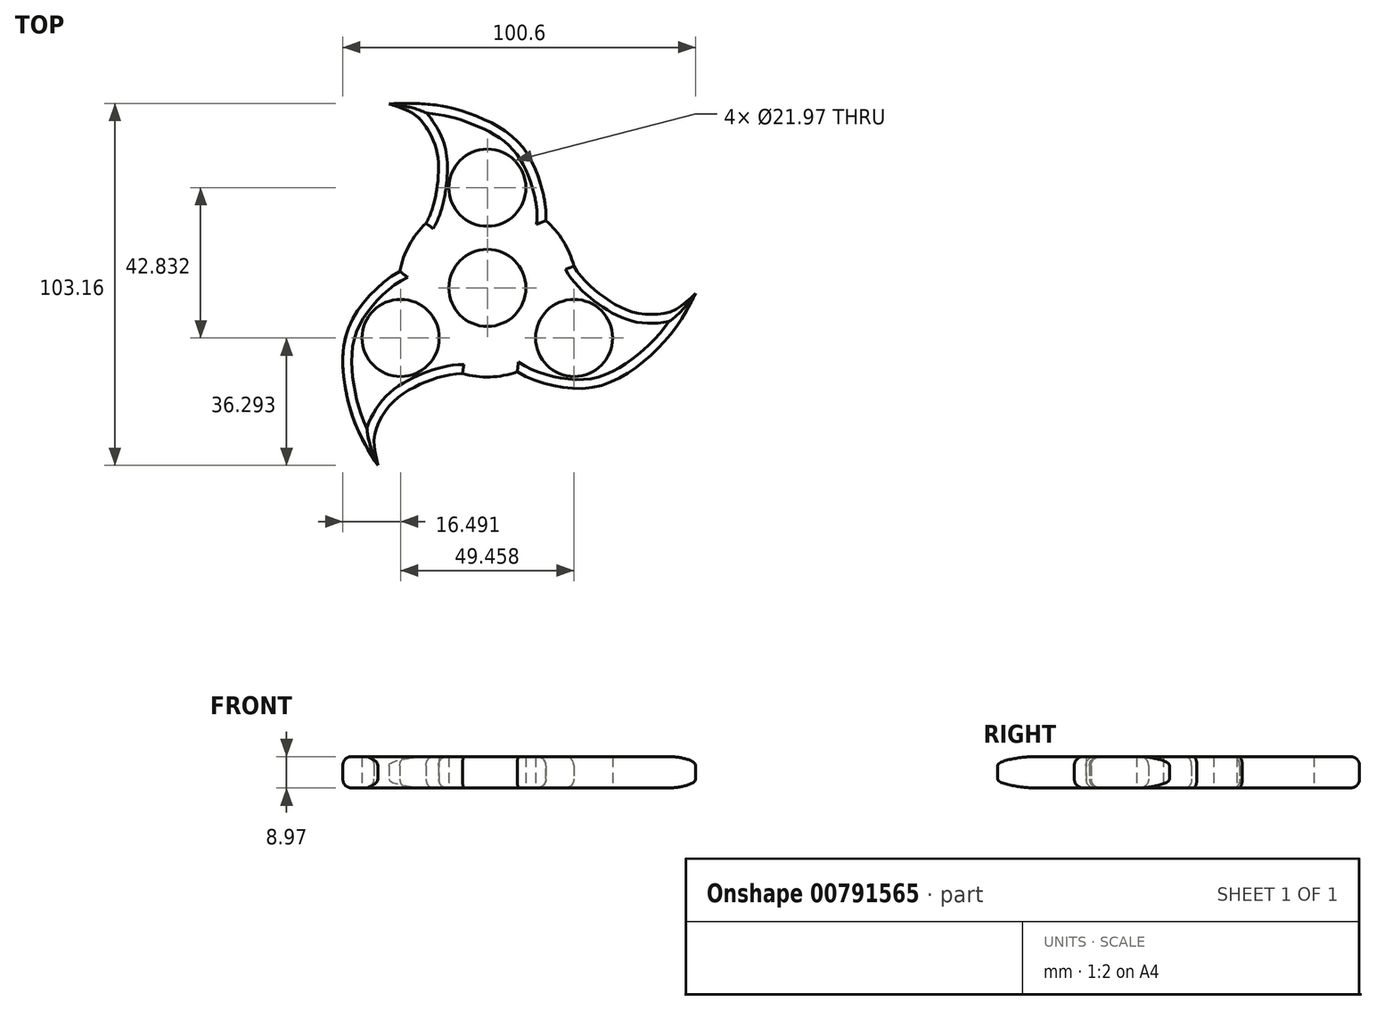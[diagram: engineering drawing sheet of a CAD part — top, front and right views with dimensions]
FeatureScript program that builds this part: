
annotation { "Feature Type Name" : "Feature", "Feature Type Description" : "" }
export const myFeature = defineFeature(function(context is Context, id is Id, definition is map)
    precondition{}
    {
        {
            var Q0;
            Q0=qCreatedBy(makeId("Top.planeOp"),FACE);
            var sketch = newSketch(context, id + "F0", { "sketchPlane" : qUnion([Q0])});
            skCircle(sketch, "E0", {"center": v(0, 0) * mm, "radius": 10.99 * mm});
            skCircle(sketch, "E1", {"center": v(0, 0) * mm, "radius": 25.4 * mm});
            skLineSegment(sketch, "E2", {"start": v(-2.48, 0) * mm, "end": v(2.46, 0) * mm, "construction": true});
            skLineSegment(sketch, "E3", {"start": v(0, 2.4) * mm, "end": v(0, -2.3) * mm});
            skFitSpline(sketch, "E4", {"points": [v(-28.09, 52.42) * mm, v(-3.88, 49.24) * mm, v(11.33, 38.29) * mm, v(16.65, 19.18) * mm], "startDerivative": vector(97.17, 5.55) * mm, "endDerivative": vector(-4.1, -37) * mm});
            skFitSpline(sketch, "E5", {"points": [v(-28.09, 52.42) * mm, v(-18.22, 46.88) * mm, v(-14.67, 39.95) * mm, v(-14.26, 29.21) * mm, v(-17.48, 18.43) * mm], "startDerivative": vector(77.17, -22.5) * mm, "endDerivative": vector(-20.17, -35.42) * mm});
            skCircle(sketch, "E6", {"center": v(0, 28.55) * mm, "radius": 10.99 * mm});
            skLineSegment(sketch, "E7", {"start": v(-14.26, 29.21) * mm, "end": v(-10.99, 28.48) * mm});
            skLineSegment(sketch, "E8", {"start": v(-10.99, 28.48) * mm, "end": v(10.99, 28.55) * mm});
            skLineSegment(sketch, "E9", {"start": v(10.99, 28.55) * mm, "end": v(15.2, 29.52) * mm});
            skCircle(sketch, "E10.1.0", {"center": v(-24.73, -14.28) * mm, "radius": 10.99 * mm});
            skLineSegment(sketch, "E10.1.1", {"start": v(-19.17, -23.75) * mm, "end": v(-30.22, -4.76) * mm});
            skCircle(sketch, "E10.2.0", {"center": v(24.73, -14.28) * mm, "radius": 10.99 * mm});
            skLineSegment(sketch, "E10.2.1", {"start": v(30.16, -4.73) * mm, "end": v(19.24, -23.8) * mm});
            skFitSpline(sketch, "E11", {"points": [v(59.38, -1.59) * mm, v(44.52, -20.97) * mm, v(27.42, -28.66) * mm, v(8.2, -23.72) * mm], "startDerivative": vector(-43.77, -86.93) * mm, "endDerivative": vector(-30, 22.04) * mm});
            skFitSpline(sketch, "E12", {"points": [v(59.38, -1.59) * mm, v(49.64, -7.37) * mm, v(41.86, -6.98) * mm, v(32.36, -1.97) * mm, v(24.63, 6.21) * mm], "startDerivative": vector(-58.07, -55.57) * mm, "endDerivative": vector(-20.59, 35.18) * mm});
            skFitSpline(sketch, "E13", {"points": [v(-31.22, -50.57) * mm, v(-40.57, -28.03) * mm, v(-38.69, -9.37) * mm, v(-24.8, 4.8) * mm], "startDerivative": vector(-53.4, 81.37) * mm, "endDerivative": vector(34.09, 14.95) * mm});
            skFitSpline(sketch, "E14", {"points": [v(-31.22, -50.57) * mm, v(-31.35, -39.26) * mm, v(-27.13, -32.72) * mm, v(-18.04, -27) * mm, v(-7.09, -24.4) * mm], "startDerivative": vector(-19.1, 78.08) * mm, "endDerivative": vector(40.76, 0.24) * mm});
            skLineSegment(sketch, "E15", {"start": v(0, 28.55) * mm, "end": v(-0.09, 54.32) * mm, "construction": true});
            skLineSegment(sketch, "E16", {"start": v(59.38, -1.59) * mm, "end": v(6.76, 43.4) * mm, "construction": true});
            skSolve(sketch);
        }
        {
            var Q0;
            Q0 = qSketchRegion(id + "F0", true);
            extrude(context, id + "F1", {"entities" : qUnion([Q0]), "depth" : 8.97 * mm, "offsetDistance" : 25.4 * mm});
        }
        {
            var Q0;
            Q0=makeQuery(id+"F1.opExtrude","CAP_EDGE",EDGE,{"disambiguationData":[OSD([sQuery(id+"F0.wireOp",EDGE,"E5")])],"isStart":false});
            var Q1;
            Q1=makeQuery(id+"F1.opExtrude","CAP_EDGE",EDGE,{"disambiguationData":[OSD([sQuery(id+"F0.wireOp",EDGE,"E5")])],"isStart":true});
            var Q2;
            Q2=makeQuery(id+"F1.opExtrude","CAP_EDGE",EDGE,{"disambiguationData":[OSD([sQuery(id+"F0.wireOp",EDGE,"E4")])],"isStart":false});
            var Q3;
            {var subQ0=sQuery(id+"F0.wireOp",EDGE,"E1");Q3=makeQuery(id+"F1.opExtrude","CAP_EDGE",EDGE,{"disambiguationData":[OSD([subQ0]),TDD([makeQuery(id+"F0.imprint","IMPRINT",EDGE,{"disambiguationData":[TD([[makeQuery(id+"F0.imprint","INTERSECT",VERTEX,{"derivedFrom":[subQ0,sQuery(id+"F0.wireOp",EDGE,"E4")]}),1.0]])],"derivedFrom":subQ0})])],"isStart":false});}
            var Q4;
            Q4=makeQuery(id+"F1.opExtrude","CAP_EDGE",EDGE,{"disambiguationData":[OSD([sQuery(id+"F0.wireOp",EDGE,"E12")])],"isStart":false});
            var Q5;
            Q5=makeQuery(id+"F1.opExtrude","CAP_EDGE",EDGE,{"disambiguationData":[OSD([sQuery(id+"F0.wireOp",EDGE,"E11")])],"isStart":false});
            var Q6;
            {var subQ0=sQuery(id+"F0.wireOp",EDGE,"E1");Q6=makeQuery(id+"F1.opExtrude","CAP_EDGE",EDGE,{"disambiguationData":[OSD([subQ0]),TDD([makeQuery(id+"F0.imprint","IMPRINT",EDGE,{"disambiguationData":[TD([[makeQuery(id+"F0.imprint","INTERSECT",VERTEX,{"derivedFrom":[subQ0,sQuery(id+"F0.wireOp",EDGE,"E14")]}),-1.0]])],"derivedFrom":subQ0})])],"isStart":false});}
            var Q7;
            Q7=makeQuery(id+"F1.opExtrude","CAP_EDGE",EDGE,{"disambiguationData":[OSD([sQuery(id+"F0.wireOp",EDGE,"E14")])],"isStart":false});
            var Q8;
            Q8=makeQuery(id+"F1.opExtrude","CAP_EDGE",EDGE,{"disambiguationData":[OSD([sQuery(id+"F0.wireOp",EDGE,"E11")])],"isStart":true});
            var Q9;
            {var subQ0=sQuery(id+"F0.wireOp",EDGE,"E1");Q9=makeQuery(id+"F1.opExtrude","CAP_EDGE",EDGE,{"disambiguationData":[OSD([subQ0]),TDD([makeQuery(id+"F0.imprint","IMPRINT",EDGE,{"disambiguationData":[TD([[makeQuery(id+"F0.imprint","INTERSECT",VERTEX,{"derivedFrom":[subQ0,sQuery(id+"F0.wireOp",EDGE,"E14")]}),-1.0]])],"derivedFrom":subQ0})])],"isStart":true});}
            var Q10;
            Q10=makeQuery(id+"F1.opExtrude","CAP_EDGE",EDGE,{"disambiguationData":[OSD([sQuery(id+"F0.wireOp",EDGE,"E14")])],"isStart":true});
            var Q11;
            Q11=makeQuery(id+"F1.opExtrude","CAP_EDGE",EDGE,{"disambiguationData":[OSD([sQuery(id+"F0.wireOp",EDGE,"E13")])],"isStart":false});
            var Q12;
            Q12=makeQuery(id+"F1.opExtrude","CAP_EDGE",EDGE,{"disambiguationData":[OSD([sQuery(id+"F0.wireOp",EDGE,"E13")])],"isStart":true});
            var Q13;
            {var subQ0=sQuery(id+"F0.wireOp",EDGE,"E1");Q13=makeQuery(id+"F1.opExtrude","CAP_EDGE",EDGE,{"disambiguationData":[OSD([subQ0]),TDD([makeQuery(id+"F0.imprint","IMPRINT",EDGE,{"disambiguationData":[TD([[makeQuery(id+"F0.imprint","INTERSECT",VERTEX,{"derivedFrom":[subQ0,sQuery(id+"F0.wireOp",EDGE,"E5")]}),-1.0]])],"derivedFrom":subQ0})])],"isStart":false});}
            var Q14;
            {var subQ0=sQuery(id+"F0.wireOp",EDGE,"E1");Q14=makeQuery(id+"F1.opExtrude","CAP_EDGE",EDGE,{"disambiguationData":[OSD([subQ0]),TDD([makeQuery(id+"F0.imprint","IMPRINT",EDGE,{"disambiguationData":[TD([[makeQuery(id+"F0.imprint","INTERSECT",VERTEX,{"derivedFrom":[subQ0,sQuery(id+"F0.wireOp",EDGE,"E5")]}),-1.0]])],"derivedFrom":subQ0})])],"isStart":true});}
            var Q15;
            Q15=makeQuery(id+"F1.opExtrude","CAP_EDGE",EDGE,{"disambiguationData":[OSD([sQuery(id+"F0.wireOp",EDGE,"E4")])],"isStart":true});
            var Q16;
            {var subQ0=sQuery(id+"F0.wireOp",EDGE,"E1");Q16=makeQuery(id+"F1.opExtrude","CAP_EDGE",EDGE,{"disambiguationData":[OSD([subQ0]),TDD([makeQuery(id+"F0.imprint","IMPRINT",EDGE,{"disambiguationData":[TD([[makeQuery(id+"F0.imprint","INTERSECT",VERTEX,{"derivedFrom":[subQ0,sQuery(id+"F0.wireOp",EDGE,"E4")]}),1.0]])],"derivedFrom":subQ0})])],"isStart":true});}
            var Q17;
            Q17=makeQuery(id+"F1.opExtrude","CAP_EDGE",EDGE,{"disambiguationData":[OSD([sQuery(id+"F0.wireOp",EDGE,"E12")])],"isStart":true});
            fillet(context, id + "F2", {"entities" : qUnion([Q0, Q1, Q2, Q3, Q4, Q5, Q6, Q7, Q8, Q9, Q10, Q11, Q12, Q13, Q14, Q15, Q16, Q17]), "radius" : 2.54 * mm, "tangentPropagation" : true, "allowEdgeOverflow" : false});
        }
    });
